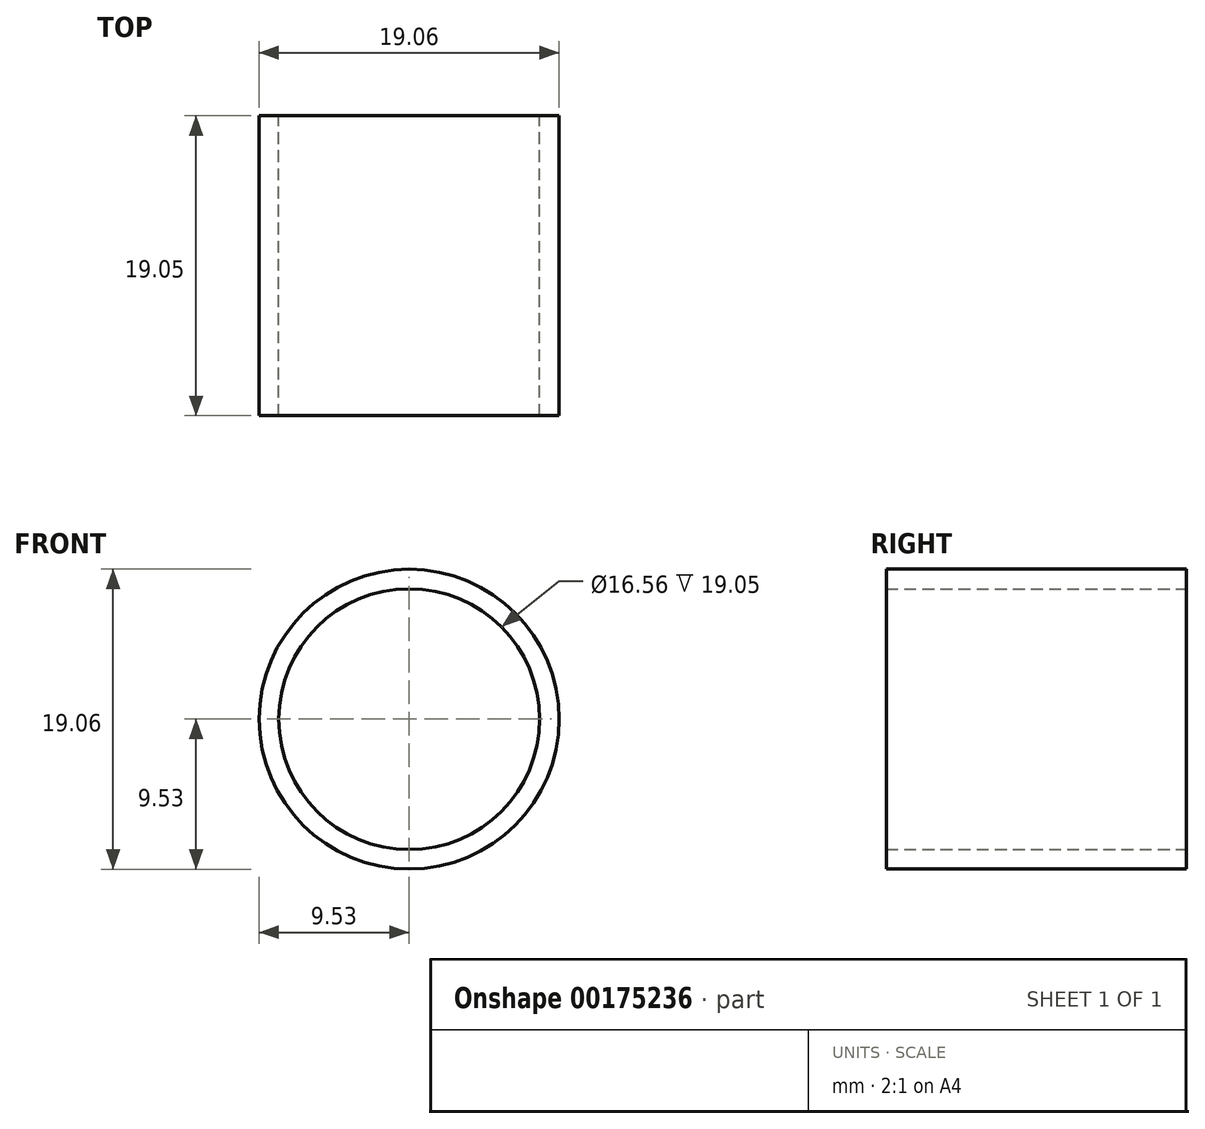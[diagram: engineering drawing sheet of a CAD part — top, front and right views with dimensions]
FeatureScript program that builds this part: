
annotation { "Feature Type Name" : "Feature", "Feature Type Description" : "" }
export const myFeature = defineFeature(function(context is Context, id is Id, definition is map)
    precondition{}
    {
        {
            var Q0;
            Q0=qCreatedBy(makeId("Front.planeOp"),FACE);
            var sketch = newSketch(context, id + "F0", { "sketchPlane" : qUnion([Q0])});
            skCircle(sketch, "E0", {"center": v(0, 0) * mm, "radius": 9.53 * mm});
            skCircle(sketch, "E1", {"center": v(0, 0) * mm, "radius": 8.28 * mm});
            skSolve(sketch);
        }
        {
            var Q0;
            Q0=makeQuery(id+"F0.imprint","IMPRINT",FACE,{"disambiguationData":[TD([[makeQuery(id+"F0.imprint","IMPRINT",EDGE,{"derivedFrom":sQuery(id+"F0.wireOp",EDGE,"E0")}),1.0]])]});
            extrude(context, id + "F1", {"entities" : qUnion([Q0]), "depth" : 19.05 * mm});
        }
    });
